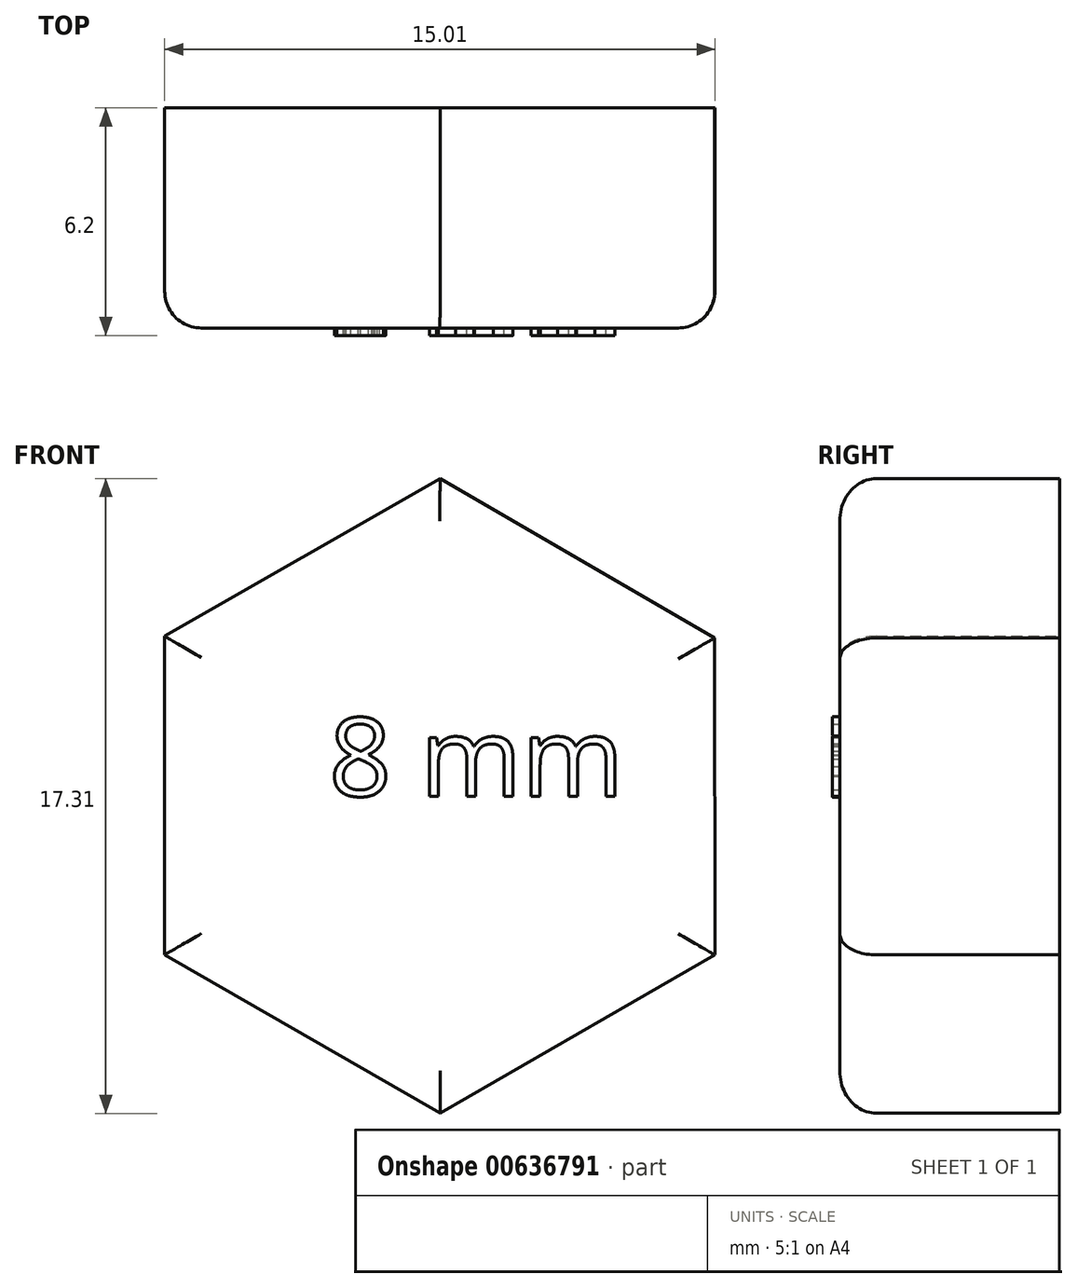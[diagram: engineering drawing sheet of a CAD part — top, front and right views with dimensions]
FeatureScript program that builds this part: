
annotation { "Feature Type Name" : "Feature", "Feature Type Description" : "" }
export const myFeature = defineFeature(function(context is Context, id is Id, definition is map)
    precondition{}
    {
        {
            var Q0;
            Q0=qCreatedBy(makeId("Front.planeOp"),FACE);
            var sketch = newSketch(context, id + "F0", { "sketchPlane" : qUnion([Q0])});
            skLineSegment(sketch, "E0", {"start": v(7.5, 20.05) * mm, "end": v(7.5, -17.65) * mm, "construction": true});
            skLineSegment(sketch, "E1", {"start": v(-7.5, 19.83) * mm, "end": v(-7.5, -18.15) * mm, "construction": true});
            skLineSegment(sketch, "E2", {"start": v(32.18, 0) * mm, "end": v(0, 0) * mm});
            skLineSegment(sketch, "E3", {"start": v(0, 0) * mm, "end": v(15.93, 27.6) * mm});
            skLineSegment(sketch, "E4", {"start": v(0, 0) * mm, "end": v(-15.8, 27.35) * mm});
            skLineSegment(sketch, "E5", {"start": v(0, 0) * mm, "end": v(-30.87, 0) * mm});
            skLineSegment(sketch, "E6", {"start": v(0, 0) * mm, "end": v(-13.71, -23.75) * mm});
            skLineSegment(sketch, "E7", {"start": v(0, 0) * mm, "end": v(15.83, -27.42) * mm});
            skPoint(sketch, "E8", {"position": v(7.5, 0) * mm});
            skSolve(sketch);
        }
        {
            var Q0;
            Q0=qCreatedBy(makeId("Right.planeOp"),FACE);
            var sketch = newSketch(context, id + "F1", { "sketchPlane" : qUnion([Q0])});
            skLineSegment(sketch, "E9", {"start": v(-63.91, 0) * mm, "end": v(61.67, 0) * mm, "construction": true});
            skSolve(sketch);
        }
        {
            var Q0;
            Q0=qCreatedBy(makeId("Front.planeOp"),FACE);
            var sketch = newSketch(context, id + "F2", { "sketchPlane" : qUnion([Q0])});
            skLineSegment(sketch, "E10", {"start": v(7.5, 4.31) * mm, "end": v(0, 8.66) * mm});
            skLineSegment(sketch, "E11", {"start": v(0, 8.66) * mm, "end": v(-7.5, 4.36) * mm});
            skLineSegment(sketch, "E12", {"start": v(-7.5, 4.36) * mm, "end": v(-7.5, -4.32) * mm});
            skLineSegment(sketch, "E13", {"start": v(-7.5, -4.32) * mm, "end": v(0, -8.65) * mm});
            skLineSegment(sketch, "E14", {"start": v(0, -8.65) * mm, "end": v(7.5, -4.33) * mm});
            skLineSegment(sketch, "E15", {"start": v(7.5, -4.33) * mm, "end": v(7.5, 4.31) * mm});
            skSolve(sketch);
        }
        {
            var Q0;
            Q0=makeQuery(id+"F2.imprint","IMPRINT",FACE,{"disambiguationData":[TD([[makeQuery(id+"F2.imprint","IMPRINT",EDGE,{"derivedFrom":sQuery(id+"F2.wireOp",EDGE,"E10")}),1.0]])]});
            extrude(context, id + "F3", {"entities" : qUnion([Q0]), "depth" : 6 * mm, "offsetDistance" : 25 * mm});
        }
        {
            var Q0;
            Q0=makeQuery(id+"F3.opExtrude","CAP_EDGE",EDGE,{"disambiguationData":[OSD([sQuery(id+"F2.wireOp",EDGE,"E10")])],"isStart":false});
            var Q1;
            Q1=makeQuery(id+"F3.opExtrude","CAP_EDGE",EDGE,{"disambiguationData":[OSD([sQuery(id+"F2.wireOp",EDGE,"E11")])],"isStart":false});
            var Q2;
            Q2=makeQuery(id+"F3.opExtrude","CAP_EDGE",EDGE,{"disambiguationData":[OSD([sQuery(id+"F2.wireOp",EDGE,"E12")])],"isStart":false});
            var Q3;
            Q3=makeQuery(id+"F3.opExtrude","CAP_EDGE",EDGE,{"disambiguationData":[OSD([sQuery(id+"F2.wireOp",EDGE,"E13")])],"isStart":false});
            var Q4;
            Q4=makeQuery(id+"F3.opExtrude","CAP_EDGE",EDGE,{"disambiguationData":[OSD([sQuery(id+"F2.wireOp",EDGE,"E14")])],"isStart":false});
            var Q5;
            Q5=makeQuery(id+"F3.opExtrude","CAP_EDGE",EDGE,{"disambiguationData":[OSD([sQuery(id+"F2.wireOp",EDGE,"E15")])],"isStart":false});
            fillet(context, id + "F4", {"entities" : qUnion([Q0, Q1, Q2, Q3, Q4, Q5]), "radius" : 1 * mm, "tangentPropagation" : true, "allowEdgeOverflow" : false});
        }
        {
            var Q0;
            Q0=makeQuery(id+"F3.opExtrude","CAP_FACE",FACE,{"disambiguationData":[OSD([sQuery(id+"F2.wireOp",EDGE,"E10"),sQuery(id+"F2.wireOp",EDGE,"E11"),sQuery(id+"F2.wireOp",EDGE,"E12"),sQuery(id+"F2.wireOp",EDGE,"E13"),sQuery(id+"F2.wireOp",EDGE,"E14"),sQuery(id+"F2.wireOp",EDGE,"E15")])],"isStart":false});
            var sketch = newSketch(context, id + "F5", { "sketchPlane" : qUnion([Q0])});
            skText(sketch, "E16", { "text": "8 mm", "fontName": "OpenSans-Regular.ttf"});
            const initialGuessF5  = {"E16": [-0.00303, 0, 1, 0, 0.00215]};
            skSetInitialGuess(sketch, initialGuessF5);
            skSolve(sketch);
        }
        {
            var Q0;
            Q0 = qSketchRegion(id + "F5", true);
            extrude(context, id + "F6", {"entities" : qUnion([Q0]), "operationType" : NewBodyOperationType.ADD, "depth" : .2 * mm, "offsetDistance" : 25 * mm});
        }
    });
